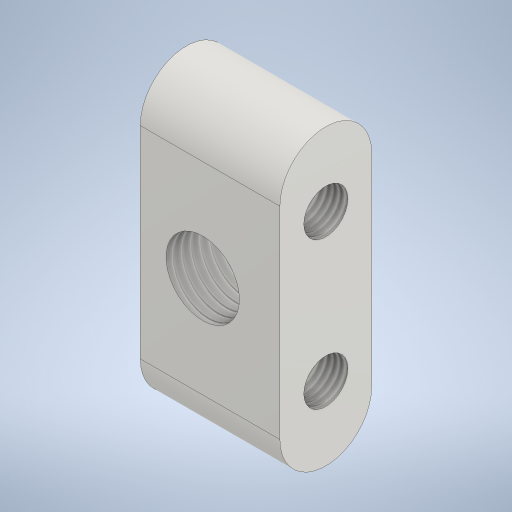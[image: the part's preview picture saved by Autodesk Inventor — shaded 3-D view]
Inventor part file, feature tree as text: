
AUTODESK INVENTOR PART (.ipt)
format: ipt  version: 2024 (Build 280153000, 153)  size: 290,816 bytes
history: native  units: mm
features: extrude x3, sketch x3, thread x3, other x2
ambient origin geometry x8: Origin, YZ Plane, XZ Plane, XY Plane, X Axis, Y Axis, Z Axis, Center Point
bodies: Body1 (feature_tree)
feature tree (11):
  extrude  "Extrusion2"  Depth=25.0mm
  other  "Full Round Fillet1"
  other  "Full Round Fillet2"
  sketch  "Sketch3"  dims[d12=80.0mm d13=40.0mm]
  sketch  "Sketch4"  dims[d14=12.5mm d15=20.0mm d16=17.0mm d17=12.0mm d18=12.0mm d19=42.0mm d20=0.0mm d21=42.0mm d22=0.0mm d29=40.0mm d30=0.0mm d31=40.0mm d32=20.0mm d37=350.0mm d38=0.0mm d39=350.0mm d40=0.0mm]
  extrude  "Extrusion3"  Depth=40.0mm
  extrude  "Extrusion4"  Depth=12.5mm
  thread  "Thread4"  [1 undecoded]
  thread  "Thread7"  [1 undecoded]
  thread  "Thread8"  [1 undecoded]
  sketch  "Sketch2"  dims[d9=38.0mm d10=0.0mm d11=25.0mm]
note: 3 required parameter values undecoded (feature->parameter linkage not recoverable at this tier; creation-order binding heuristic only, values carry confidence <= 0.55)
